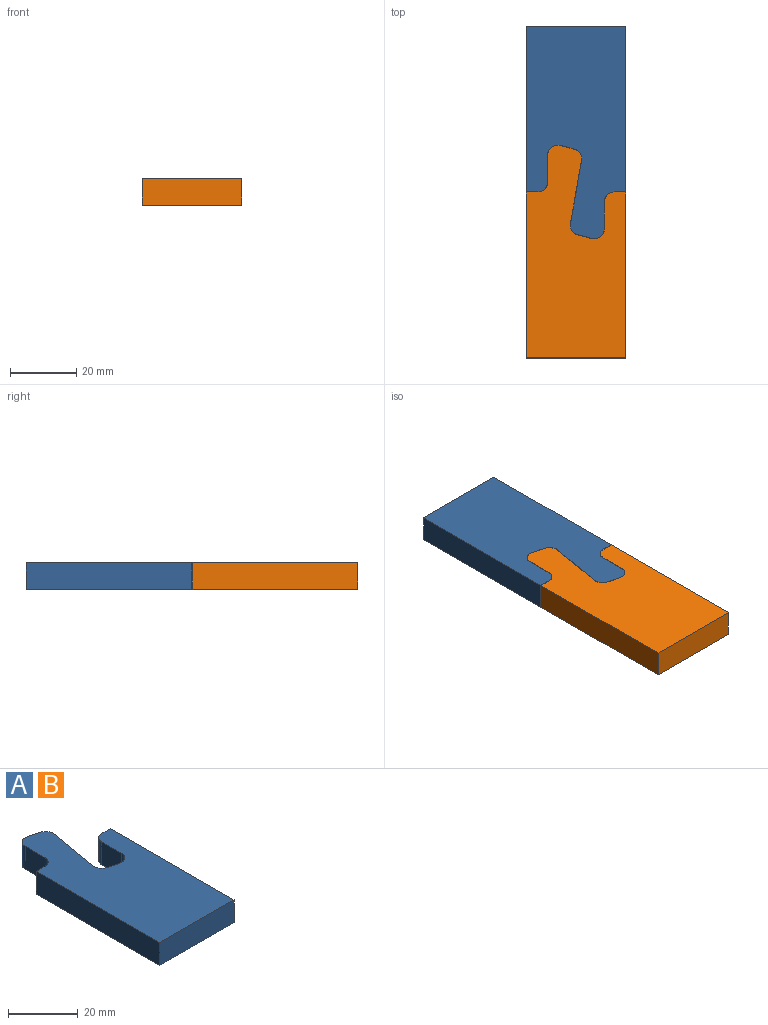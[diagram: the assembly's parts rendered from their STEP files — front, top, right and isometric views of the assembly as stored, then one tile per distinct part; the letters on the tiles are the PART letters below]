
ASSEMBLY  parts=2 mates=1
PART A: 18 faces, bbox 29.9x64.1x8 mm
  f0: plane 8.09x8mm, normal (-1,0,0), area 64.7mm2, adj f1,f15,f16,f17
  f1: cylinder r=3mm len=8mm, axis (0,0,-1), area 37.7mm2, adj f0,f2,f16,f17
  f2: plane 8x3.5mm, normal (0,1,0), area 28mm2, adj f1,f3,f16,f17
  f3: plane 50x8mm, normal (-1,0,0), area 400mm2, adj f2,f4,f16,f17
  f4: plane 29.95x8mm, normal (0,-1,0), area 239.6mm2, adj f3,f5,f16,f17
  f5: plane 50x8mm, normal (1,0,0), area 400mm2, adj f4,f6,f16,f17
  f6: plane 8x3.5mm, normal (0,1,0), area 28mm2, adj f5,f7,f16,f17
  f7: cylinder r=2.9mm len=8mm, axis (0,0,-1), area 36.4mm2, adj f6,f8,f16,f17
  f8: plane 8.1x8mm, normal (-1,0,0), area 64.8mm2, adj f7,f9,f16,f17
  f9: cylinder r=3.15mm len=8mm, axis (0,0,-1), area 46.2mm2, adj f8,f10,f16,f17
  f10: plane 8x3.97mm, normal (0.26,0.97,0), area 32.9mm2, adj f9,f11,f16,f17
  f11: cylinder r=3.15mm len=8mm, axis (0,0,-1), area 37.4mm2, adj f10,f12,f16,f17
  f12: plane 18.83x8mm, normal (0.98,-0.17,0), area 153mm2, adj f11,f13,f16,f17
  f13: cylinder r=3mm len=8mm, axis (0,0,-1), area 35.6mm2, adj f12,f14,f16,f17
  f14: plane 8x4.19mm, normal (0.26,0.97,0), area 34.7mm2, adj f13,f15,f16,f17
  f15: cylinder r=3mm len=8mm, axis (0,0,-1), area 44mm2, adj f0,f14,f16,f17
  f16: plane 64.09x29.95mm, normal (0,0,1), area 1496mm2, adj f0,f1,f2,f3,f4,f5,f6,f7
  f17: plane 64.09x29.95mm, normal (0,0,-1), area 1496mm2, adj f0,f1,f2,f3,f4,f5,f6,f7
PART B: same geometry as A
PLACE A rot(axis=(0,0,1),180deg) t=(14.38,14.24,-7.39)mm
PLACE B t=(-15.62,14.23,-7.32)mm fixed
MATE parallel B.f12 <-> A.f12  axis (0.98,-0.17,0) through (-0.63,14.26,-3.32)mm
